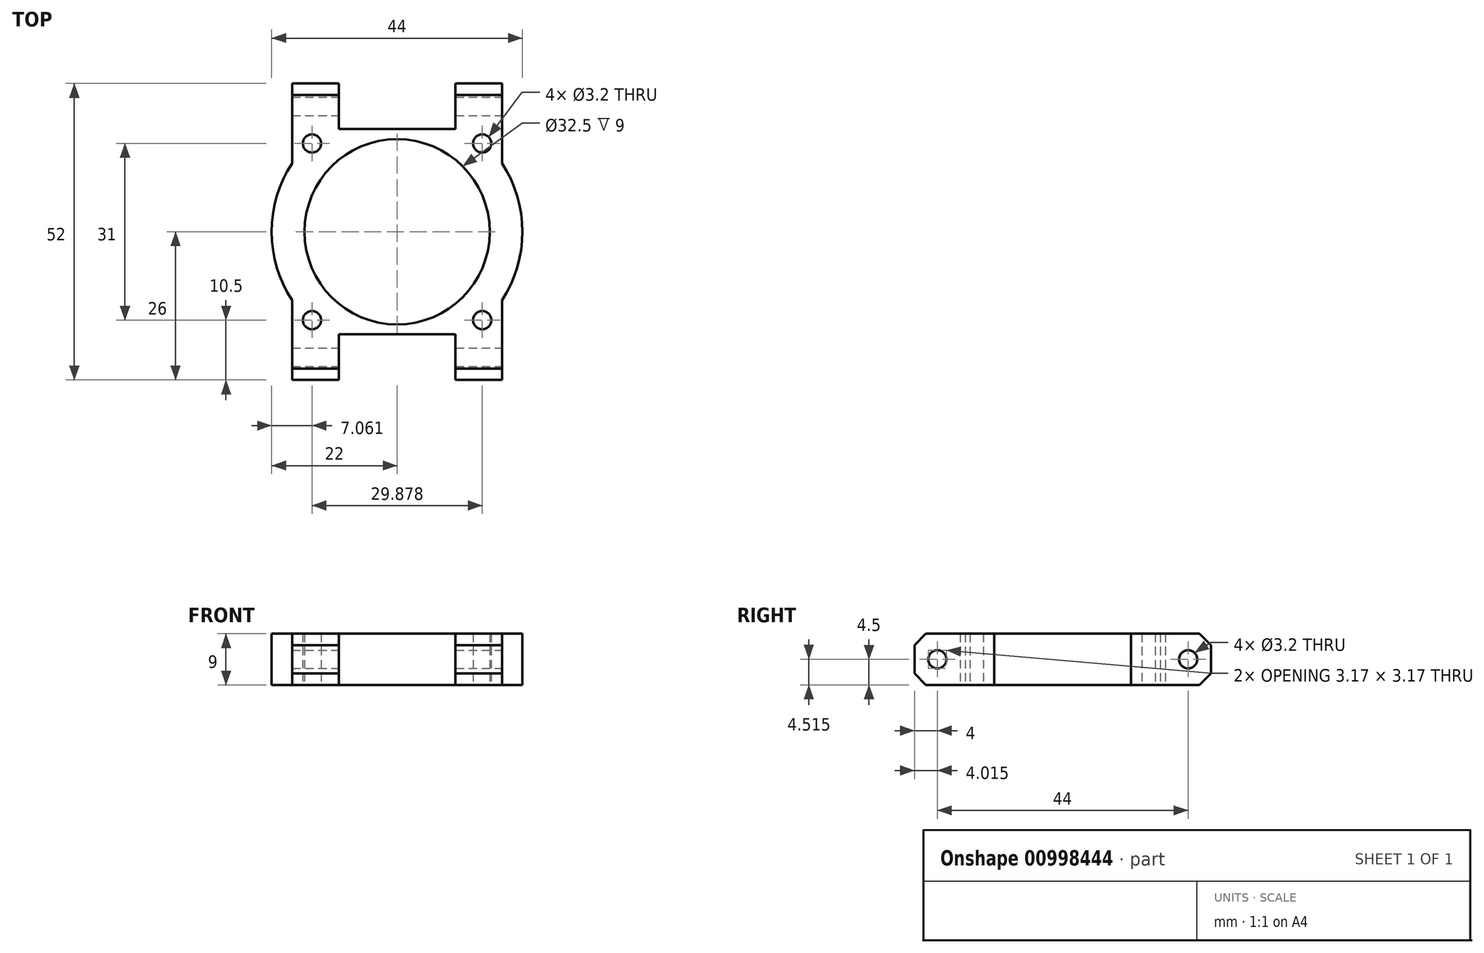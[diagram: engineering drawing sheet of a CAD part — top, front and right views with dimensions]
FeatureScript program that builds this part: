
annotation { "Feature Type Name" : "Feature", "Feature Type Description" : "" }
export const myFeature = defineFeature(function(context is Context, id is Id, definition is map)
    precondition{}
    {
        {
            var Q0;
            Q0=qCreatedBy(makeId("Top.planeOp"),FACE);
            var sketch = newSketch(context, id + "F0", { "sketchPlane" : qUnion([Q0])});
            skCircle(sketch, "E0", {"center": v(0, 0) * mm, "radius": 16.25 * mm});
            skArc(sketch, "E1", {"start": v(18.44, -12) * mm, "mid": v(22, 0) * mm, "end": v(18.44, 12) * mm});
            skLineSegment(sketch, "E2.bottom", {"start": v(18.44, 12) * mm, "end": v(10.96, 12) * mm});
            skLineSegment(sketch, "E2.top", {"start": v(18.44, 26) * mm, "end": v(-18.44, 26) * mm});
            skLineSegment(sketch, "E2.left", {"start": v(18.44, 12) * mm, "end": v(18.44, 26) * mm});
            skLineSegment(sketch, "E2.right", {"start": v(-18.44, 12) * mm, "end": v(-18.44, 26) * mm});
            skPoint(sketch, "E2.middle", {"position": v(0, 19) * mm});
            skLineSegment(sketch, "E3.bottom", {"start": v(18.44, -12) * mm, "end": v(10.96, -12) * mm});
            skLineSegment(sketch, "E3.top", {"start": v(18.44, -26) * mm, "end": v(-18.44, -26) * mm});
            skLineSegment(sketch, "E3.left", {"start": v(18.44, -12) * mm, "end": v(18.44, -26) * mm});
            skLineSegment(sketch, "E3.right", {"start": v(-18.44, -12) * mm, "end": v(-18.44, -26) * mm});
            skPoint(sketch, "E3.middle", {"position": v(0, -19) * mm});
            skLineSegment(sketch, "E4.bottom", {"start": v(10.25, 26) * mm, "end": v(-10.25, 26) * mm});
            skLineSegment(sketch, "E4.top", {"start": v(10.25, 18) * mm, "end": v(-10.25, 18) * mm});
            skLineSegment(sketch, "E4.left", {"start": v(10.25, 26) * mm, "end": v(10.25, 18) * mm});
            skLineSegment(sketch, "E4.right", {"start": v(-10.25, 26) * mm, "end": v(-10.25, 18) * mm});
            skPoint(sketch, "E4.middle", {"position": v(0, 22) * mm});
            skLineSegment(sketch, "E5.bottom", {"start": v(10.25, -26) * mm, "end": v(-10.25, -26) * mm});
            skLineSegment(sketch, "E5.top", {"start": v(10.25, -18) * mm, "end": v(-10.25, -18) * mm});
            skLineSegment(sketch, "E5.left", {"start": v(10.25, -26) * mm, "end": v(10.25, -18) * mm});
            skLineSegment(sketch, "E5.right", {"start": v(-10.25, -26) * mm, "end": v(-10.25, -18) * mm});
            skPoint(sketch, "E5.middle", {"position": v(0, -22) * mm});
            skLineSegment(sketch, "E6.trimOffspring", {"start": v(-10.96, 12) * mm, "end": v(-18.44, 12) * mm});
            skLineSegment(sketch, "E7.trimOffspring", {"start": v(-10.96, -12) * mm, "end": v(-18.44, -12) * mm});
            skArc(sketch, "E8.trimOffspring", {"start": v(-18.44, 12) * mm, "mid": v(-22, 0) * mm, "end": v(-18.44, -12) * mm});
            skPoint(sketch, "E9", {"position": v(14.94, 15.5) * mm});
            skPoint(sketch, "E10", {"position": v(-14.94, 15.5) * mm});
            skPoint(sketch, "E11", {"position": v(-14.94, -15.5) * mm});
            skPoint(sketch, "E12", {"position": v(14.94, -15.5) * mm});
            skSolve(sketch);
        }
        {
            var Q0;
            {var subQ5=sQuery(id+"F0.wireOp",EDGE,"E3.bottom");Q0=makeQuery(id+"F0.imprint","IMPRINT",FACE,{"disambiguationData":[TD([[makeQuery(id+"F0.imprint","IMPRINT",EDGE,{"derivedFrom":subQ5}),1.0]])]});}
            var Q1;
            {var subQ0=sQuery(id+"F0.wireOp",EDGE,"E6.trimOffspring");Q1=makeQuery(id+"F0.imprint","IMPRINT",FACE,{"disambiguationData":[TD([[makeQuery(id+"F0.imprint","IMPRINT",EDGE,{"derivedFrom":subQ0}),1.0]])]});}
            var Q2;
            {var subQ6=sQuery(id+"F0.wireOp",EDGE,"E2.bottom");Q2=makeQuery(id+"F0.imprint","IMPRINT",FACE,{"disambiguationData":[TD([[makeQuery(id+"F0.imprint","IMPRINT",EDGE,{"derivedFrom":subQ6}),-1.0]])]});}
            var Q3;
            Q3=makeQuery(id+"F0.imprint","IMPRINT",FACE,{"disambiguationData":[TD([[makeQuery(id+"F0.imprint","IMPRINT",EDGE,{"derivedFrom":sQuery(id+"F0.wireOp",EDGE,"E1")}),1.0]])]});
            extrude(context, id + "F1", {"entities" : qUnion([Q0, Q1, Q2, Q3]), "depth" : 9 * mm, "offsetDistance" : 25 * mm});
        }
        {
            var Q0;
            Q0=sQuery(id+"F0.wireOp",VERTEX,"E11");
            var Q1;
            Q1=sQuery(id+"F0.wireOp",VERTEX,"E12");
            var Q2;
            Q2=sQuery(id+"F0.wireOp",VERTEX,"E9");
            var Q3;
            Q3=sQuery(id+"F0.wireOp",VERTEX,"E10");
            var Q4;
            Q4=makeQuery(id+"F1.opExtrude","SWEPT_BODY",BODY,{"disambiguationData":[OSD([sQuery(id+"F0.wireOp",EDGE,"E0"),sQuery(id+"F0.wireOp",EDGE,"E1"),sQuery(id+"F0.wireOp",EDGE,"E2.top"),sQuery(id+"F0.wireOp",EDGE,"E2.left"),sQuery(id+"F0.wireOp",EDGE,"E2.right"),sQuery(id+"F0.wireOp",EDGE,"E3.top"),sQuery(id+"F0.wireOp",EDGE,"E3.left"),sQuery(id+"F0.wireOp",EDGE,"E3.right"),sQuery(id+"F0.wireOp",EDGE,"E4.top"),sQuery(id+"F0.wireOp",EDGE,"E4.left"),sQuery(id+"F0.wireOp",EDGE,"E4.right"),sQuery(id+"F0.wireOp",EDGE,"E5.top"),sQuery(id+"F0.wireOp",EDGE,"E5.left"),sQuery(id+"F0.wireOp",EDGE,"E5.right"),sQuery(id+"F0.wireOp",EDGE,"E8.trimOffspring")])]});
            hole(context, id + "F2", {"style" : HoleStyle.SIMPLE, "endStyle" : HoleEndStyle.BLIND, "oppositeDirection" : true, "holeDiameter" : 3.2 * mm, "majorDiameter" : 5 * mm, "holeDepth" : 9 * mm, "isTappedThrough" : true, "tappedDepth" : 12 * mm, "tapClearance" : 3, "locations" : qUnion([Q0, Q1, Q2, Q3]), "scope" : qUnion([Q4])});
        }
        {
            var Q0;
            Q0=makeQuery(id+"F1.opExtrude","SWEPT_FACE",FACE,{"disambiguationData":[OSD([sQuery(id+"F0.wireOp",EDGE,"E2.left")])]});
            var sketch = newSketch(context, id + "F3", { "sketchPlane" : qUnion([Q0])});
            skPoint(sketch, "E13", {"position": v(22, 4.5) * mm});
            skPoint(sketch, "E14", {"position": v(-22, 4.5) * mm});
            skSolve(sketch);
        }
        {
            var Q0;
            Q0=sQuery(id+"F3.wireOp",VERTEX,"E14");
            var Q1;
            Q1=sQuery(id+"F3.wireOp",VERTEX,"E13");
            var Q2;
            Q2=makeQuery(id+"F1.opExtrude","SWEPT_BODY",BODY,{"disambiguationData":[OSD([sQuery(id+"F0.wireOp",EDGE,"E0"),sQuery(id+"F0.wireOp",EDGE,"E1"),sQuery(id+"F0.wireOp",EDGE,"E2.top"),sQuery(id+"F0.wireOp",EDGE,"E2.left"),sQuery(id+"F0.wireOp",EDGE,"E2.right"),sQuery(id+"F0.wireOp",EDGE,"E3.top"),sQuery(id+"F0.wireOp",EDGE,"E3.left"),sQuery(id+"F0.wireOp",EDGE,"E3.right"),sQuery(id+"F0.wireOp",EDGE,"E4.top"),sQuery(id+"F0.wireOp",EDGE,"E4.left"),sQuery(id+"F0.wireOp",EDGE,"E4.right"),sQuery(id+"F0.wireOp",EDGE,"E5.top"),sQuery(id+"F0.wireOp",EDGE,"E5.left"),sQuery(id+"F0.wireOp",EDGE,"E5.right"),sQuery(id+"F0.wireOp",EDGE,"E8.trimOffspring")])]});
            hole(context, id + "F4", {"style" : HoleStyle.SIMPLE, "endStyle" : HoleEndStyle.BLIND, "holeDiameter" : 3.2 * mm, "majorDiameter" : 5 * mm, "holeDepth" : 40 * mm, "isTappedThrough" : true, "tappedDepth" : 12 * mm, "tapClearance" : 3, "locations" : qUnion([Q0, Q1]), "scope" : qUnion([Q2])});
        }
        {
            var Q0;
            {var subQ0=sQuery(id+"F0.wireOp",EDGE,"E2.top");Q0=makeQuery(id+"F1.opExtrude","CAP_EDGE",EDGE,{"disambiguationData":[OSD([subQ0]),TDD([makeQuery(id+"F0.imprint","IMPRINT",EDGE,{"disambiguationData":[TD([[makeQuery(id+"F0.imprint","INTERSECT",VERTEX,{"derivedFrom":[subQ0,sQuery(id+"F0.wireOp",EDGE,"E2.left")]}),-1.0]])],"derivedFrom":subQ0})])],"isStart":false});}
            var Q1;
            {var subQ0=sQuery(id+"F0.wireOp",EDGE,"E2.top");Q1=makeQuery(id+"F1.opExtrude","CAP_EDGE",EDGE,{"disambiguationData":[OSD([subQ0]),TDD([makeQuery(id+"F0.imprint","IMPRINT",EDGE,{"disambiguationData":[TD([[makeQuery(id+"F0.imprint","INTERSECT",VERTEX,{"derivedFrom":[subQ0,sQuery(id+"F0.wireOp",EDGE,"E2.left")]}),-1.0]])],"derivedFrom":subQ0})])],"isStart":true});}
            var Q2;
            {var subQ0=sQuery(id+"F0.wireOp",EDGE,"E2.top");Q2=makeQuery(id+"F1.opExtrude","CAP_EDGE",EDGE,{"disambiguationData":[OSD([subQ0]),TDD([makeQuery(id+"F0.imprint","IMPRINT",EDGE,{"disambiguationData":[TD([[makeQuery(id+"F0.imprint","INTERSECT",VERTEX,{"derivedFrom":[subQ0,sQuery(id+"F0.wireOp",EDGE,"E2.right")]}),1.0]])],"derivedFrom":subQ0})])],"isStart":false});}
            var Q3;
            {var subQ0=sQuery(id+"F0.wireOp",EDGE,"E2.top");Q3=makeQuery(id+"F1.opExtrude","CAP_EDGE",EDGE,{"disambiguationData":[OSD([subQ0]),TDD([makeQuery(id+"F0.imprint","IMPRINT",EDGE,{"disambiguationData":[TD([[makeQuery(id+"F0.imprint","INTERSECT",VERTEX,{"derivedFrom":[subQ0,sQuery(id+"F0.wireOp",EDGE,"E2.right")]}),1.0]])],"derivedFrom":subQ0})])],"isStart":true});}
            var Q4;
            {var subQ0=sQuery(id+"F0.wireOp",EDGE,"E3.top");Q4=makeQuery(id+"F1.opExtrude","CAP_EDGE",EDGE,{"disambiguationData":[OSD([subQ0]),TDD([makeQuery(id+"F0.imprint","IMPRINT",EDGE,{"disambiguationData":[TD([[makeQuery(id+"F0.imprint","INTERSECT",VERTEX,{"derivedFrom":[subQ0,sQuery(id+"F0.wireOp",EDGE,"E3.right")]}),1.0]])],"derivedFrom":subQ0})])],"isStart":false});}
            var Q5;
            {var subQ0=sQuery(id+"F0.wireOp",EDGE,"E3.top");Q5=makeQuery(id+"F1.opExtrude","CAP_EDGE",EDGE,{"disambiguationData":[OSD([subQ0]),TDD([makeQuery(id+"F0.imprint","IMPRINT",EDGE,{"disambiguationData":[TD([[makeQuery(id+"F0.imprint","INTERSECT",VERTEX,{"derivedFrom":[subQ0,sQuery(id+"F0.wireOp",EDGE,"E3.left")]}),-1.0]])],"derivedFrom":subQ0})])],"isStart":false});}
            var Q6;
            {var subQ0=sQuery(id+"F0.wireOp",EDGE,"E3.top");Q6=makeQuery(id+"F1.opExtrude","CAP_EDGE",EDGE,{"disambiguationData":[OSD([subQ0]),TDD([makeQuery(id+"F0.imprint","IMPRINT",EDGE,{"disambiguationData":[TD([[makeQuery(id+"F0.imprint","INTERSECT",VERTEX,{"derivedFrom":[subQ0,sQuery(id+"F0.wireOp",EDGE,"E3.left")]}),-1.0]])],"derivedFrom":subQ0})])],"isStart":true});}
            var Q7;
            {var subQ0=sQuery(id+"F0.wireOp",EDGE,"E3.top");Q7=makeQuery(id+"F1.opExtrude","CAP_EDGE",EDGE,{"disambiguationData":[OSD([subQ0]),TDD([makeQuery(id+"F0.imprint","IMPRINT",EDGE,{"disambiguationData":[TD([[makeQuery(id+"F0.imprint","INTERSECT",VERTEX,{"derivedFrom":[subQ0,sQuery(id+"F0.wireOp",EDGE,"E3.right")]}),1.0]])],"derivedFrom":subQ0})])],"isStart":true});}
            chamfer(context, id + "F5", {"entities" : qUnion([Q0, Q1, Q2, Q3, Q4, Q5, Q6, Q7]), "width" : 2 * mm, "tangentPropagation" : true});
        }
    });
